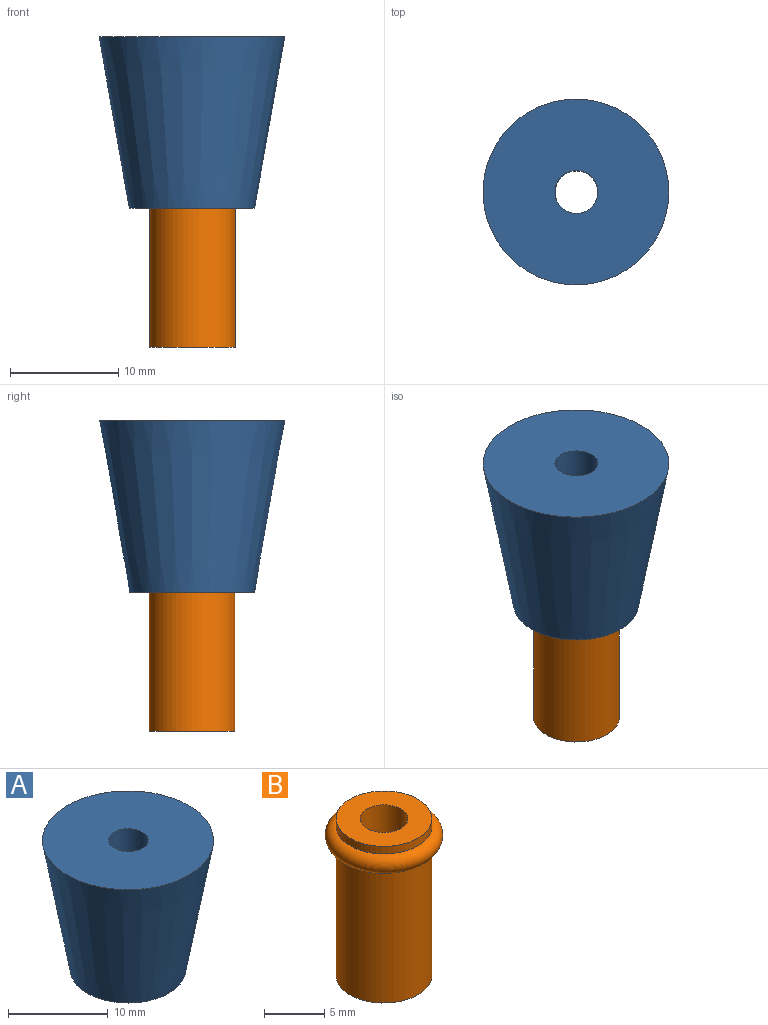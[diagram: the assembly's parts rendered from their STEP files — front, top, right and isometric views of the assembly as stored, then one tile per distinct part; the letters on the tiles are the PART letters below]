
ASSEMBLY  parts=2 mates=1
PART A: 8 faces, bbox 17.2x17.2x15.9 mm
  f0: plane 17.16x17.16mm, normal (0,0,1), area 218.9mm2, adj f5,f7
  f1: plane 11.56x11.56mm, normal (0,0,-1), area 36.1mm2, adj f6,f7
  f2: torus R=4.37mm, axis (0,0,1), area 85.7mm2, adj f3,f6
  f3: cylinder r=4.37mm len=8.73mm, axis (0,0,1), area 20.9mm2, adj f2,f4
  f4: plane 8.73x8.73mm, normal (0,0,-1), area 47.5mm2, adj f3,f5
  f5: cylinder r=1.98mm len=12.54mm, axis (0,0,1), area 156.4mm2, adj f0,f4
  f6: cylinder r=4.68mm len=9.37mm, axis (0,0,1), area 20.5mm2, adj f1,f2
  f7: cone r=8.89mm half-angle=10deg, axis (0,0,1), area 727.3mm2, adj f0,f1
PART B: 6 faces, bbox 10.5x10.5x15.9 mm
  f0: torus R=3.97mm, axis (0,0,-1), area 79.6mm2, adj f1,f5
  f1: cylinder r=3.97mm len=13.34mm, axis (0,0,-1), area 332.5mm2, adj f0,f2
  f2: plane 7.94x7.94mm, normal (0,0,-1), area 37.1mm2, adj f1,f3
  f3: cylinder r=1.98mm len=15.88mm, axis (0,0,-1), area 197.9mm2, adj f2,f4
  f4: plane 7.94x7.94mm, normal (0,0,1), area 37.1mm2, adj f3,f5
  f5: cylinder r=3.97mm len=7.94mm, axis (0,0,-1), area 19mm2, adj f0,f4
PLACE A t=(-4.92,-4.77,4.76)mm
PLACE B t=(-0.55,-4.77,2.56)mm
MATE cylindrical A.f3 <-> B.f0  axis (0,0,1) through (-0.55,-4.77,7.34)mm
